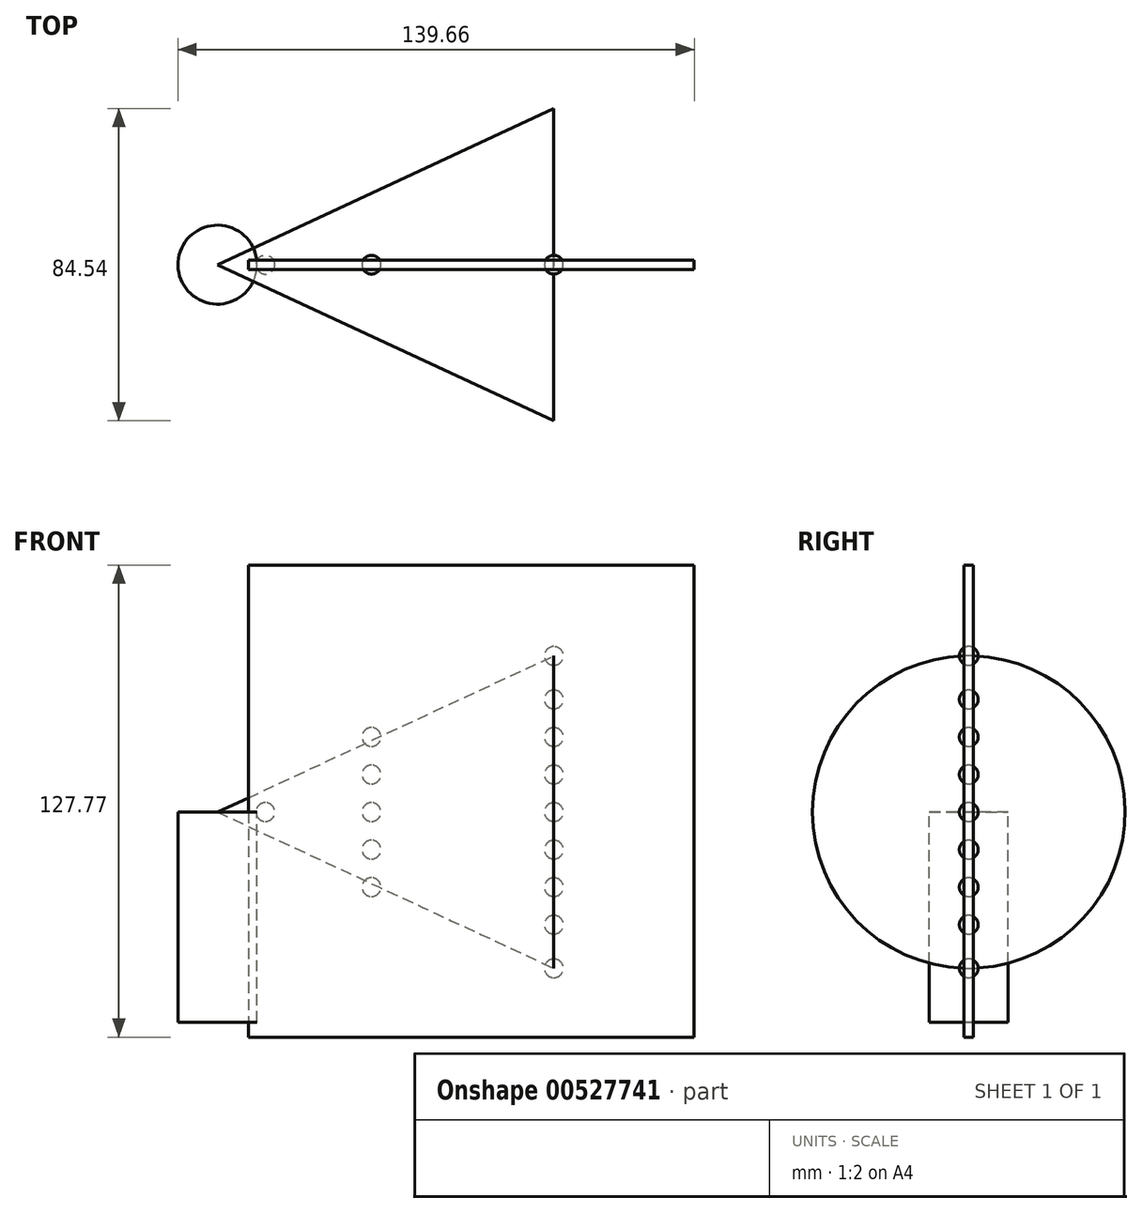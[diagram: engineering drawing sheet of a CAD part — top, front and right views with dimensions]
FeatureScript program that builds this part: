
annotation { "Feature Type Name" : "Feature", "Feature Type Description" : "" }
export const myFeature = defineFeature(function(context is Context, id is Id, definition is map)
    precondition{}
    {
        {
            var Q0;
            Q0=qCreatedBy(makeId("Top.planeOp"),FACE);
            var sketch = newSketch(context, id + "F0", { "sketchPlane" : qUnion([Q0])});
            skLineSegment(sketch, "E0", {"start": v(0, 0) * mm, "end": v(91, 42.27) * mm});
            skLineSegment(sketch, "E1", {"start": v(91, 42.27) * mm, "end": v(91, 0) * mm});
            skLineSegment(sketch, "E2", {"start": v(91, 0) * mm, "end": v(0, 0) * mm});
            skSolve(sketch);
        }
        {
            var Q0;
            Q0=makeQuery(id+"F0.imprint","IMPRINT",FACE,{"disambiguationData":[TD([[makeQuery(id+"F0.imprint","IMPRINT",EDGE,{"derivedFrom":sQuery(id+"F0.wireOp",EDGE,"E0")}),-1.0]])]});
            var Q1;
            Q1=sQuery(id+"F0.wireOp",EDGE,"E2");
            revolve(context, id + "F1", {"entities" : qUnion([Q0]), "axis" : qUnion([Q1]), "revolveType" : RevolveType.FULL});
        }
        {
            var Q0;
            Q0=qCreatedBy(makeId("Top.planeOp"),FACE);
            var sketch = newSketch(context, id + "F2", { "sketchPlane" : qUnion([Q0])});
            skCircle(sketch, "E3", {"center": v(0, 0) * mm, "radius": 10.7 * mm});
            skSolve(sketch);
        }
        {
            var Q0;
            Q0=makeQuery(id+"F2.imprint","IMPRINT",FACE,{"disambiguationData":[TD([[makeQuery(id+"F2.imprint","IMPRINT",EDGE,{"derivedFrom":sQuery(id+"F2.wireOp",EDGE,"E3")}),1.0]])]});
            extrude(context, id + "F3", {"entities" : qUnion([Q0]), "oppositeDirection" : true, "depth" : 56.9 * mm, "offsetDistance" : 25.4 * mm});
        }
        {
            var Q0;
            Q0=qCreatedBy(makeId("Front.planeOp"),FACE);
            var sketch = newSketch(context, id + "F4", { "sketchPlane" : qUnion([Q0])});
            skLineSegment(sketch, "E4.bottom", {"start": v(8.35, 66.87) * mm, "end": v(128.97, 66.87) * mm});
            skLineSegment(sketch, "E4.top", {"start": v(8.35, -60.9) * mm, "end": v(128.97, -60.9) * mm});
            skLineSegment(sketch, "E4.left", {"start": v(8.35, 66.87) * mm, "end": v(8.35, -60.9) * mm});
            skLineSegment(sketch, "E4.right", {"start": v(128.97, 66.87) * mm, "end": v(128.97, -60.9) * mm});
            skSolve(sketch);
        }
        {
            var Q0;
            Q0=makeQuery(id+"F4.imprint","IMPRINT",FACE,{"disambiguationData":[TD([[makeQuery(id+"F4.imprint","IMPRINT",EDGE,{"derivedFrom":sQuery(id+"F4.wireOp",EDGE,"E4.bottom")}),-1.0]])]});
            extrude(context, id + "F5", {"entities" : qUnion([Q0]), "depth" : 1.27 * mm, "offsetDistance" : 25.4 * mm, "hasSecondDirection" : true, "secondDirectionOppositeDirection" : true, "secondDirectionDepth" : 1.27 * mm});
        }
        {
            var Q0;
            Q0=makeQuery(id+"F1.opRevolve","SWEPT_FACE",FACE,{"disambiguationData":[OSD([sQuery(id+"F0.wireOp",EDGE,"E1")])]});
            var sketch = newSketch(context, id + "F6", { "sketchPlane" : qUnion([Q0])});
            skArc(sketch, "E5", {"start": v(0, 39.73) * mm, "mid": v(2.54, 42.27) * mm, "end": v(0, 44.81) * mm});
            skArc(sketch, "E6", {"start": v(0, 27.94) * mm, "mid": v(2.54, 30.48) * mm, "end": v(0, 33.02) * mm});
            skArc(sketch, "E7", {"start": v(0, 17.78) * mm, "mid": v(2.54, 20.32) * mm, "end": v(0, 22.86) * mm});
            skArc(sketch, "E8", {"start": v(0, 7.62) * mm, "mid": v(2.54, 10.16) * mm, "end": v(0, 12.7) * mm});
            skArc(sketch, "E9", {"start": v(0, -2.54) * mm, "mid": v(2.54, 0) * mm, "end": v(0, 2.54) * mm});
            skArc(sketch, "E10.MirrorC", {"start": v(0, -39.73) * mm, "mid": v(2.54, -42.27) * mm, "end": v(0, -44.81) * mm});
            skArc(sketch, "E11.MirrorC", {"start": v(0, -27.94) * mm, "mid": v(2.54, -30.48) * mm, "end": v(0, -33.02) * mm});
            skArc(sketch, "E12.MirrorC", {"start": v(0, -17.78) * mm, "mid": v(2.54, -20.32) * mm, "end": v(0, -22.86) * mm});
            skArc(sketch, "E13.MirrorC", {"start": v(0, -7.62) * mm, "mid": v(2.54, -10.16) * mm, "end": v(0, -12.7) * mm});
            skLineSegment(sketch, "E14", {"start": v(0, 42.27) * mm, "end": v(0, 39.73) * mm, "construction": true});
            skLineSegment(sketch, "E15", {"start": v(0, 44.81) * mm, "end": v(0, 39.73) * mm});
            skLineSegment(sketch, "E16.trimOffspring", {"start": v(0, -39.73) * mm, "end": v(0, -44.81) * mm});
            skLineSegment(sketch, "E17.trimOffspring", {"start": v(0, -27.94) * mm, "end": v(0, -30.48) * mm, "construction": true});
            skLineSegment(sketch, "E18.trimOffspring", {"start": v(0, -17.78) * mm, "end": v(0, -22.86) * mm, "construction": true});
            skLineSegment(sketch, "E19.trimOffspring", {"start": v(0, -7.62) * mm, "end": v(0, -12.7) * mm, "construction": true});
            skLineSegment(sketch, "E20.trimOffspring", {"start": v(0, 2.54) * mm, "end": v(0, -2.54) * mm, "construction": true});
            skLineSegment(sketch, "E21.trimOffspring", {"start": v(0, -7.62) * mm, "end": v(0, -12.7) * mm});
            skLineSegment(sketch, "E22.trimOffspring", {"start": v(0, 2.54) * mm, "end": v(0, -2.54) * mm});
            skLineSegment(sketch, "E23.trimOffspring", {"start": v(0, 12.7) * mm, "end": v(0, 7.62) * mm, "construction": true});
            skLineSegment(sketch, "E24.trimOffspring", {"start": v(0, 12.7) * mm, "end": v(0, 7.62) * mm});
            skLineSegment(sketch, "E25.trimOffspring", {"start": v(0, 22.86) * mm, "end": v(0, 17.78) * mm, "construction": true});
            skLineSegment(sketch, "E26.trimOffspring", {"start": v(0, 22.86) * mm, "end": v(0, 17.78) * mm});
            skLineSegment(sketch, "E27.trimOffspring", {"start": v(0, 33.02) * mm, "end": v(0, 27.94) * mm, "construction": true});
            skLineSegment(sketch, "E28.trimOffspring", {"start": v(0, 33.02) * mm, "end": v(0, 27.94) * mm});
            skPoint(sketch, "E29.orphan", {"position": v(0, 49.79) * mm});
            skLineSegment(sketch, "E30.trimOffspring", {"start": v(0, -27.94) * mm, "end": v(0, -33.02) * mm});
            skLineSegment(sketch, "E31.trimOffspring", {"start": v(0, -17.78) * mm, "end": v(0, -22.86) * mm});
            skSolve(sketch);
        }
        {
            var Q0;
            Q0 = qSketchRegion(id + "F6", true);
            var Q1;
            Q1=sQuery(id+"F6.wireOp",EDGE,"E5");
            var Q2;
            Q2=sQuery(id+"F6.wireOp",EDGE,"E6");
            var Q3;
            Q3=sQuery(id+"F6.wireOp",EDGE,"E7");
            var Q4;
            Q4=sQuery(id+"F6.wireOp",EDGE,"E14");
            revolve(context, id + "F7", {"entities" : qUnion([Q0]), "surfaceEntities" : qUnion([Q1, Q2, Q3]), "axis" : qUnion([Q4]), "revolveType" : RevolveType.FULL});
        }
        {
            var Q0;
            Q0=qCreatedBy(makeId("Right.planeOp"),FACE);
            cPlane(context, id + "F8", {"entities" : qUnion([Q0]), "cplaneType" : CPlaneType.OFFSET, "offset" : 41.66 * mm, "width" : 152.4 * mm, "height" : 152.4 * mm});
        }
        {
            var Q0;
            Q0=qCreatedBy(id+"F8.planeOp",FACE);
            var sketch = newSketch(context, id + "F9", { "sketchPlane" : qUnion([Q0])});
            skArc(sketch, "E32.0.0", {"start": v(0, 17.78) * mm, "mid": v(2.54, 20.32) * mm, "end": v(0, 22.86) * mm});
            skLineSegment(sketch, "E32.0.1", {"start": v(0, 22.86) * mm, "end": v(0, 17.78) * mm});
            skArc(sketch, "E33.0.0", {"start": v(0, 7.62) * mm, "mid": v(2.54, 10.16) * mm, "end": v(0, 12.7) * mm});
            skLineSegment(sketch, "E33.0.1", {"start": v(0, 12.7) * mm, "end": v(0, 7.62) * mm});
            skArc(sketch, "E34.0.0", {"start": v(0, -2.54) * mm, "mid": v(2.54, 0) * mm, "end": v(0, 2.54) * mm});
            skLineSegment(sketch, "E34.0.1", {"start": v(0, 2.54) * mm, "end": v(0, -2.54) * mm});
            skArc(sketch, "E35.0.0", {"start": v(0, -12.7) * mm, "mid": v(2.54, -10.16) * mm, "end": v(0, -7.62) * mm});
            skLineSegment(sketch, "E35.0.1", {"start": v(0, -7.62) * mm, "end": v(0, -12.7) * mm});
            skArc(sketch, "E36.0.0", {"start": v(0, -22.86) * mm, "mid": v(2.54, -20.32) * mm, "end": v(0, -17.78) * mm});
            skLineSegment(sketch, "E36.0.1", {"start": v(0, -17.78) * mm, "end": v(0, -22.86) * mm});
            skSolve(sketch);
        }
        {
            var Q0;
            Q0 = qSketchRegion(id + "F9", true);
            var Q1;
            Q1=sQuery(id+"F9.wireOp",EDGE,"E35.0.1");
            revolve(context, id + "F10", {"entities" : qUnion([Q0]), "axis" : qUnion([Q1]), "revolveType" : RevolveType.FULL});
        }
        {
            var Q0;
            Q0=qCreatedBy(makeId("Right.planeOp"),FACE);
            cPlane(context, id + "F11", {"entities" : qUnion([Q0]), "cplaneType" : CPlaneType.OFFSET, "offset" : 12.95 * mm, "width" : 152.4 * mm, "height" : 152.4 * mm});
        }
        {
            var Q0;
            Q0=qCreatedBy(id+"F11.planeOp",FACE);
            var sketch = newSketch(context, id + "F12", { "sketchPlane" : qUnion([Q0])});
            skArc(sketch, "E37.0.0", {"start": v(0, -2.54) * mm, "mid": v(2.54, 0) * mm, "end": v(0, 2.54) * mm});
            skLineSegment(sketch, "E37.0.1", {"start": v(0, 2.54) * mm, "end": v(0, -2.54) * mm});
            skSolve(sketch);
        }
        {
            var Q0;
            Q0 = qSketchRegion(id + "F12", true);
            var Q1;
            Q1=sQuery(id+"F12.wireOp",EDGE,"E37.0.1");
            revolve(context, id + "F13", {"entities" : qUnion([Q0]), "axis" : qUnion([Q1]), "revolveType" : RevolveType.FULL});
        }
    });
